# Revit family: 111014001025286
name_source: partatom
category: Modelos genéricos
revit_build: Autodesk Revit 2018 (Build: 20190510_1515(x64)
units: mm (PartAtom-declared; Revit-internal decimal feet)

## family parameters
Compartido = No
Corte con vacíos al cargar = No
Cota de conector redondo = Diámetro de uso
Puede alojar armadura = No
Punto de cálculo de habitación = No
Se basa en plano de trabajo = No
Siempre vertical = No
Tipo de pieza = Normal

## types (1)
- BARRA CLOSET PP C/ACERO 1" CAFE TIRA 1.5MT
    Aplicacion = Barra de  cortina para baños y uso en closet.
    Color = Café
    Descripción = Barra closet pp c/acero 1" 1.5M
    Dimension = 23 mm  [stored 0.0754593 ft]
    Empresa = CNP SPA.
    Espesor = 0 mm  [stored 0 ft]
    Largo = 1500 mm  [stored 4.92126 ft]
    Material = PP con acero cafe
    Modelo = BARRA CLOSET PP C/ACERO 1"
    Nombre SKU = BARRA CLOSET PP C/ACERO 1" CAFE TIRA 1.5MT
    Num SKUs = 111014001025286
    URL = https://www.empresascnp.cl
    Unidad = Tira 1.50 mts.
    Url Ficha tecnica = https://empresascnp.cl
    Uso = Se instala en los baños para colgar la cortina de las duchas.
En el caso de ser instalado en el closet, se utiliza para colgar la ropa

note: [stored X ft] marks values corroborated as IEEE doubles in the binary element streams (Revit-internal decimal feet)

## geometry (parser evidence)
native form markers: Sweep x2
no freeform markers — native parametric forms only
